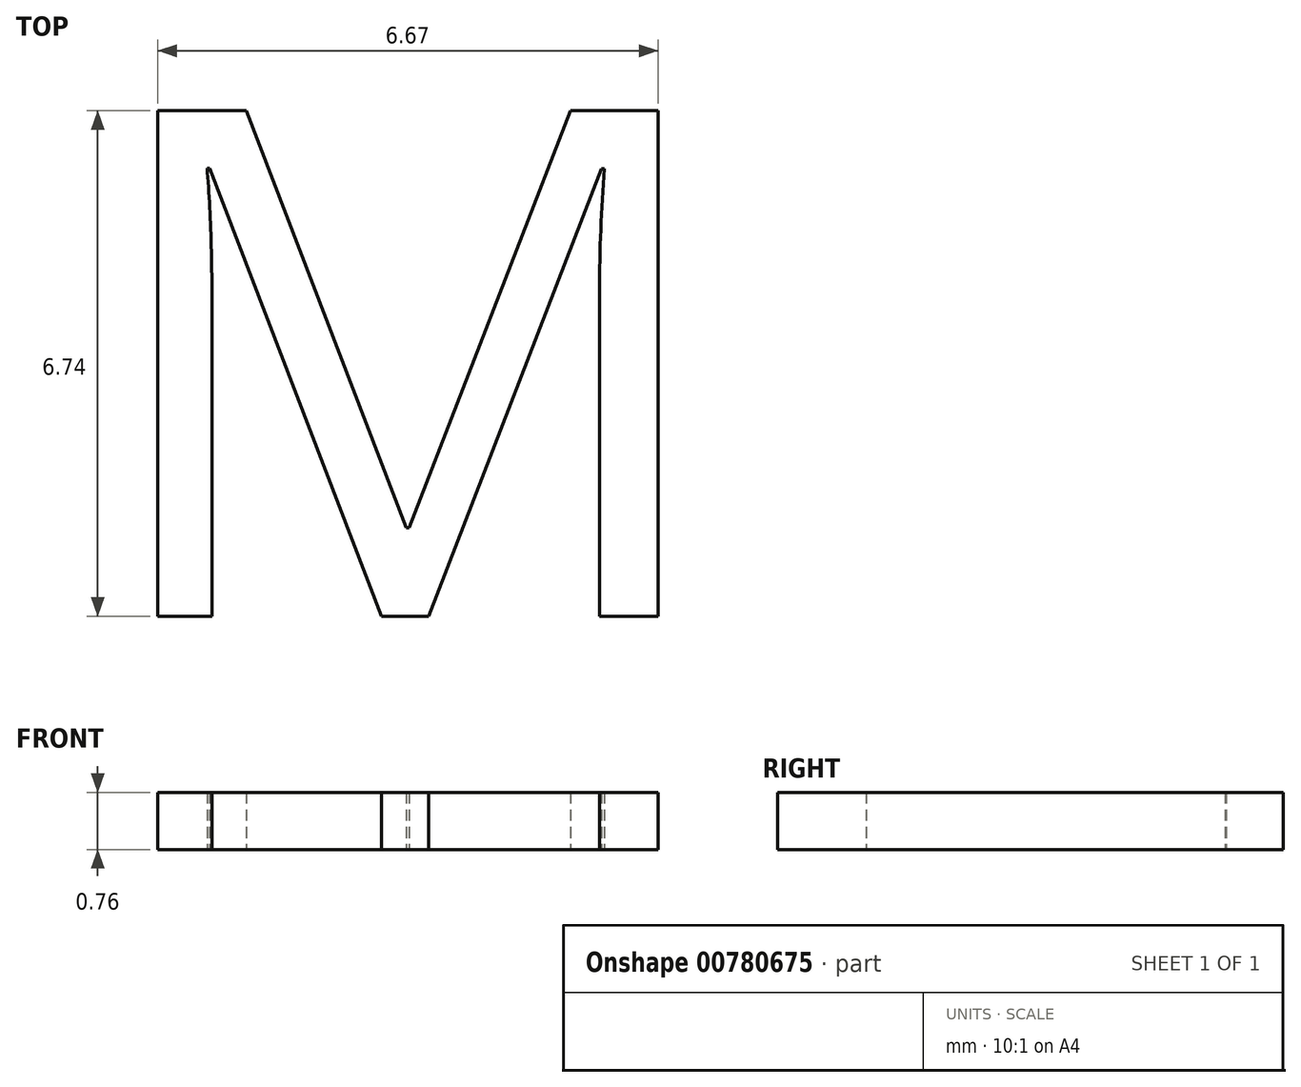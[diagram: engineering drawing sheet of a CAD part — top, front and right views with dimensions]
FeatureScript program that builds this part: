
annotation { "Feature Type Name" : "Feature", "Feature Type Description" : "" }
export const myFeature = defineFeature(function(context is Context, id is Id, definition is map)
    precondition{}
    {
        {
            var Q0;
            Q0=qCreatedBy(makeId("Top.planeOp"),FACE);
            var sketch = newSketch(context, id + "F0", { "sketchPlane" : qUnion([Q0])});
            skText(sketch, "E0", { "text": "M\n", "fontName": "OpenSans-Regular.ttf"});
            const initialGuessF0  = {"E0": [-0.0082, 0, 1, 0, 0.0068]};
            skSetInitialGuess(sketch, initialGuessF0);
            skSolve(sketch);
        }
        {
            var Q0;
            Q0 = qSketchRegion(id + "F0", true);
            extrude(context, id + "F1", {"entities" : qUnion([Q0]), "depth" : 0.76 * mm, "offsetDistance" : 25.4 * mm});
        }
    });
